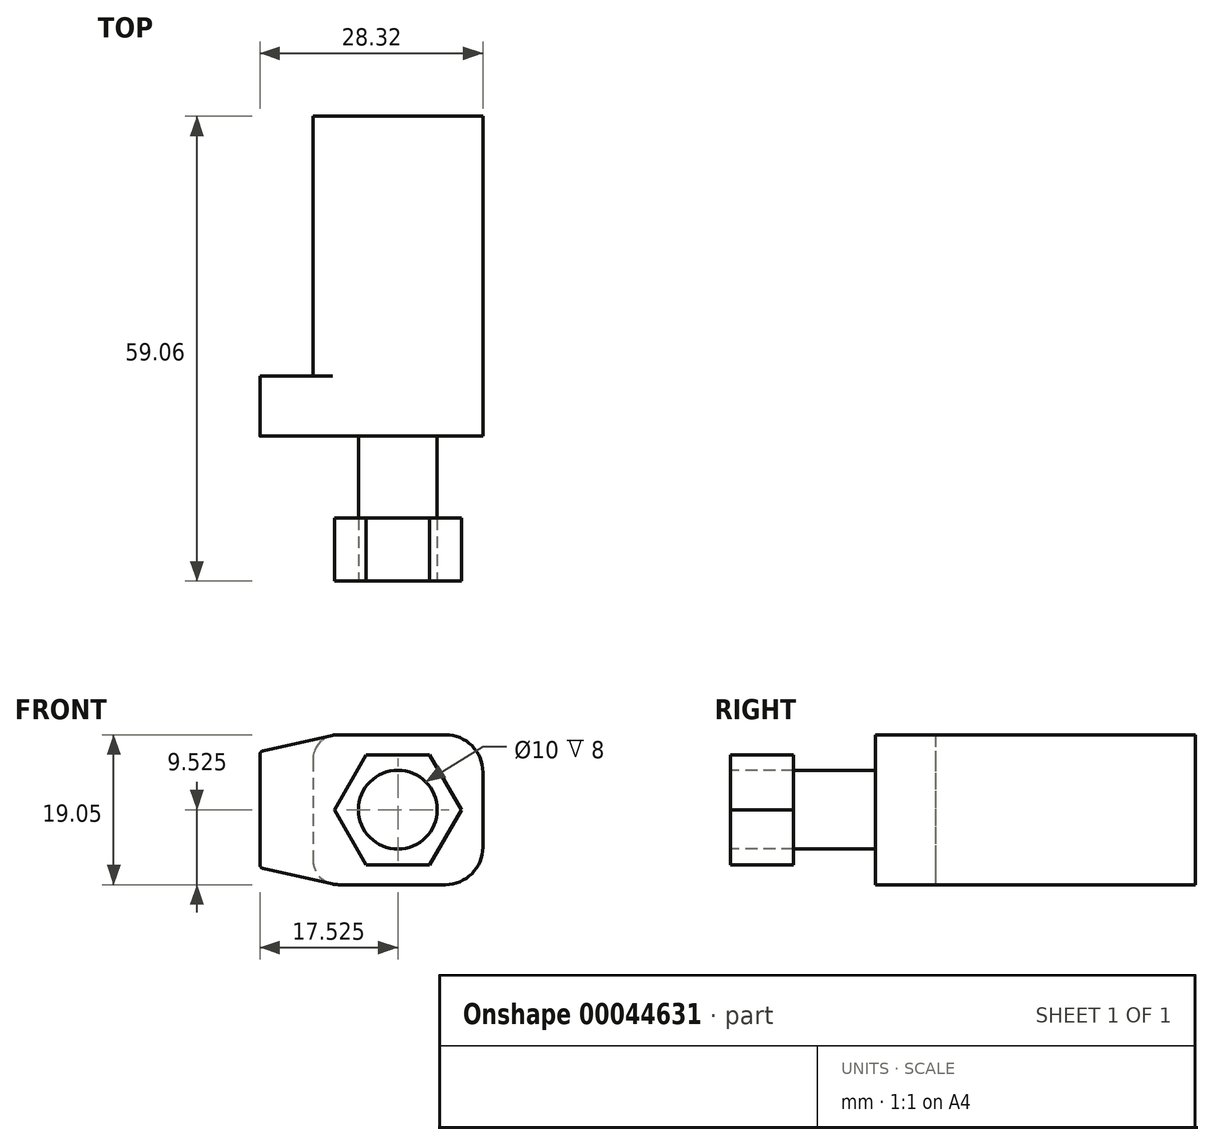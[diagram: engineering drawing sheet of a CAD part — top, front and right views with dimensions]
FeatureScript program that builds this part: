
annotation { "Feature Type Name" : "Feature", "Feature Type Description" : "" }
export const myFeature = defineFeature(function(context is Context, id is Id, definition is map)
    precondition{}
    {
        {
            var Q0;
            Q0=qCreatedBy(makeId("Front.planeOp"),FACE);
            var sketch = newSketch(context, id + "F0", { "sketchPlane" : qUnion([Q0])});
            skLineSegment(sketch, "E0.bottom", {"start": v(3.18, 0) * mm, "end": v(16.83, 0) * mm});
            skLineSegment(sketch, "E0.top", {"start": v(3.18, -19.05) * mm, "end": v(16.83, -19.05) * mm});
            skLineSegment(sketch, "E0.left", {"start": v(0, -3.18) * mm, "end": v(0, -15.88) * mm});
            skLineSegment(sketch, "E0.right", {"start": v(21.59, -4.76) * mm, "end": v(21.59, -14.29) * mm});
            skPoint(sketch, "E1.visualSharp", {"position": v(0, 0) * mm});
            skArc(sketch, "E1.filletArc", {"start": v(3.18, 0) * mm, "mid": v(0.93, -0.93) * mm, "end": v(0, -3.18) * mm});
            skPoint(sketch, "E2.visualSharp", {"position": v(0, -19.05) * mm});
            skArc(sketch, "E2.filletArc", {"start": v(0, -15.88) * mm, "mid": v(0.93, -18.12) * mm, "end": v(3.18, -19.05) * mm});
            skPoint(sketch, "E3.visualSharp", {"position": v(21.59, 0) * mm});
            skArc(sketch, "E3.filletArc", {"start": v(21.59, -4.76) * mm, "mid": v(20.2, -1.4) * mm, "end": v(16.83, 0) * mm});
            skPoint(sketch, "E4.visualSharp", {"position": v(21.59, -19.05) * mm});
            skArc(sketch, "E4.filletArc", {"start": v(16.83, -19.05) * mm, "mid": v(20.2, -17.66) * mm, "end": v(21.59, -14.29) * mm});
            skSolve(sketch);
        }
        {
            var Q0;
            Q0 = qSketchRegion(id + "F0", true);
            extrude(context, id + "F1", {"entities" : qUnion([Q0]), "oppositeDirection" : true, "depth" : 40.64 * mm});
        }
        {
            var Q0;
            Q0=makeQuery(id+"F1.opExtrude","CAP_FACE",FACE,{"disambiguationData":[OSD([sQuery(id+"F0.wireOp",EDGE,"E0.bottom"),sQuery(id+"F0.wireOp",EDGE,"E0.top"),sQuery(id+"F0.wireOp",EDGE,"E0.left"),sQuery(id+"F0.wireOp",EDGE,"E0.right"),sQuery(id+"F0.wireOp",EDGE,"E1.filletArc"),sQuery(id+"F0.wireOp",EDGE,"E2.filletArc"),sQuery(id+"F0.wireOp",EDGE,"E3.filletArc"),sQuery(id+"F0.wireOp",EDGE,"E4.filletArc")])],"isStart":true});
            var sketch = newSketch(context, id + "F2", { "sketchPlane" : qUnion([Q0])});
            skCircle(sketch, "E5", {"center": v(10.8, -9.53) * mm, "radius": 5 * mm});
            skLineSegment(sketch, "E6", {"start": v(0, -9.53) * mm, "end": v(21.59, -9.53) * mm, "construction": true});
            skLineSegment(sketch, "E7", {"start": v(10.8, 0) * mm, "end": v(10.8, -19.05) * mm, "construction": true});
            skSolve(sketch);
        }
        {
            var Q0;
            Q0 = qSketchRegion(id + "F2", true);
            extrude(context, id + "F3", {"entities" : qUnion([Q0]), "operationType" : NewBodyOperationType.ADD, "depth" : 18.41 * mm});
        }
        {
            var Q0;
            Q0=makeQuery(id+"F1.opExtrude","CAP_FACE",FACE,{"disambiguationData":[OSD([sQuery(id+"F0.wireOp",EDGE,"E0.bottom"),sQuery(id+"F0.wireOp",EDGE,"E0.top"),sQuery(id+"F0.wireOp",EDGE,"E0.left"),sQuery(id+"F0.wireOp",EDGE,"E0.right"),sQuery(id+"F0.wireOp",EDGE,"E1.filletArc"),sQuery(id+"F0.wireOp",EDGE,"E2.filletArc"),sQuery(id+"F0.wireOp",EDGE,"E3.filletArc"),sQuery(id+"F0.wireOp",EDGE,"E4.filletArc")])],"isStart":true});
            var sketch = newSketch(context, id + "F4", { "sketchPlane" : qUnion([Q0])});
            skLineSegment(sketch, "E8", {"start": v(2.48, -0.08) * mm, "end": v(-6.33, -2.04) * mm});
            skLineSegment(sketch, "E9", {"start": v(-6.73, -2.54) * mm, "end": v(-6.73, -16.51) * mm});
            skLineSegment(sketch, "E10", {"start": v(-6.33, -17) * mm, "end": v(2.48, -18.97) * mm});
            skPoint(sketch, "E11.visualSharp", {"position": v(-6.73, -2.13) * mm});
            skArc(sketch, "E11.filletArc", {"start": v(-6.33, -2.04) * mm, "mid": v(-6.62, -2.22) * mm, "end": v(-6.73, -2.54) * mm});
            skPoint(sketch, "E12.visualSharp", {"position": v(-6.73, -16.92) * mm});
            skArc(sketch, "E12.filletArc", {"start": v(-6.73, -16.51) * mm, "mid": v(-6.62, -16.83) * mm, "end": v(-6.33, -17) * mm});
            skLineSegment(sketch, "E13", {"start": v(-6.73, -9.53) * mm, "end": v(10.8, -9.53) * mm, "construction": true});
            skLineSegment(sketch, "E14.0", {"start": v(0, -3.18) * mm, "end": v(0, -15.88) * mm});
            skArc(sketch, "E15", {"start": v(0, -15.88) * mm, "mid": v(0.7, -17.86) * mm, "end": v(2.48, -18.97) * mm});
            skArc(sketch, "E16", {"start": v(2.48, -0.08) * mm, "mid": v(0.7, -1.19) * mm, "end": v(0, -3.17) * mm});
            skSolve(sketch);
        }
        {
            var Q0;
            Q0 = qSketchRegion(id + "F4", true);
            extrude(context, id + "F5", {"entities" : qUnion([Q0]), "operationType" : NewBodyOperationType.ADD, "oppositeDirection" : true, "depth" : 7.62 * mm});
        }
        {
            var Q0;
            Q0=makeQuery(id+"F3.opExtrude","CAP_FACE",FACE,{"disambiguationData":[OSD([sQuery(id+"F2.wireOp",EDGE,"E5")])],"isStart":false});
            var sketch = newSketch(context, id + "F6", { "sketchPlane" : qUnion([Q0])});
            skCircle(sketch, "E17.cCircle", {"center": v(10.8, -9.53) * mm, "radius": 6.99 * mm, "construction": true});
            skLineSegment(sketch, "E17.0", {"start": v(6.76, -2.54) * mm, "end": v(14.83, -2.54) * mm});
            skLineSegment(sketch, "E17.1", {"start": v(14.83, -2.54) * mm, "end": v(18.86, -9.53) * mm});
            skLineSegment(sketch, "E17.2", {"start": v(18.86, -9.53) * mm, "end": v(14.83, -16.51) * mm});
            skLineSegment(sketch, "E17.3", {"start": v(14.83, -16.51) * mm, "end": v(6.76, -16.51) * mm});
            skLineSegment(sketch, "E17.4", {"start": v(6.76, -16.51) * mm, "end": v(2.73, -9.53) * mm});
            skLineSegment(sketch, "E17.5", {"start": v(2.73, -9.53) * mm, "end": v(6.76, -2.54) * mm});
            skPoint(sketch, "E17.0.midPoint", {"position": v(10.8, -2.54) * mm});
            skCircle(sketch, "E18.0", {"center": v(10.8, -9.53) * mm, "radius": 5 * mm});
            skSolve(sketch);
        }
        {
            var Q0;
            Q0 = qSketchRegion(id + "F6", true);
            extrude(context, id + "F7", {"entities" : qUnion([Q0]), "oppositeDirection" : true, "depth" : 8 * mm});
        }
    });
